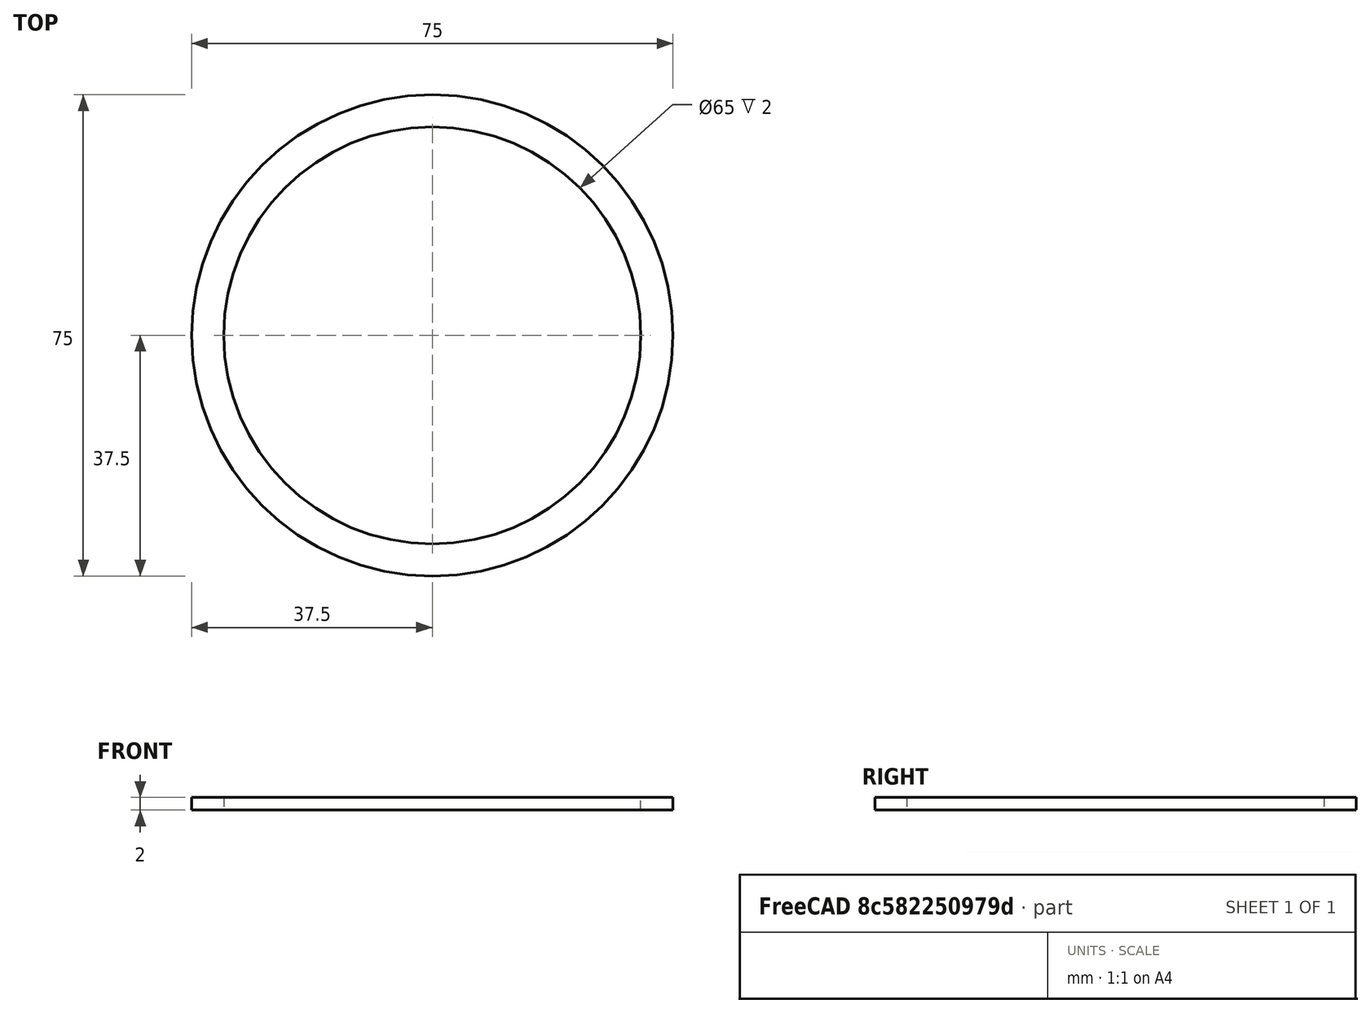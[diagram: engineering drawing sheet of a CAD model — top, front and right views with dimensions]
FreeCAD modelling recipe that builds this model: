
FCSTD DOCUMENT  (FreeCAD 0.19R24276 (Git))
Label: Ring_d65_d75_h2
License: All rights reserved
LicenseURL: http://en.wikipedia.org/wiki/All_rights_reserved
objects: Sketcher::SketchObject×1, PartDesign::Pad×1, PartDesign::Body×1
note: 4 computed .brp shape members not serialized (recipe doc carries the construction recipe); baked Part::Feature solids carry a one-line shape summary decoded from their .brp

FEATURE [Sketcher::SketchObject] Sketch
  FullyConstrained = true
  MapMode = 5
  Support = -> [XY_Plane]
  sketch-geometry (2):
    g0: Circle CenterX=0 CenterY=0 CenterZ=0 NormalX=0 NormalY=0 NormalZ=1 AngleXU=0 Radius=32.5
    g1: Circle CenterX=0 CenterY=0 CenterZ=0 NormalX=0 NormalY=0 NormalZ=1 AngleXU=0 Radius=37.5
  constraints (4):
    c: Coincident(g0,g-1)
    c: Coincident(g1,g0)
    c: Diameter(g0) = 65
    c: Diameter(g1) = 75
FEATURE [PartDesign::Pad] Pad
  Direction = (1,1,1)
  Length = 2
  Length2 = 100
  Profile = -> Sketch
  Type = 0
FEATURE [PartDesign::Body] Body
  Group = -> [Sketch,Pad]
  Origin = -> Origin
  Tip = -> Pad
